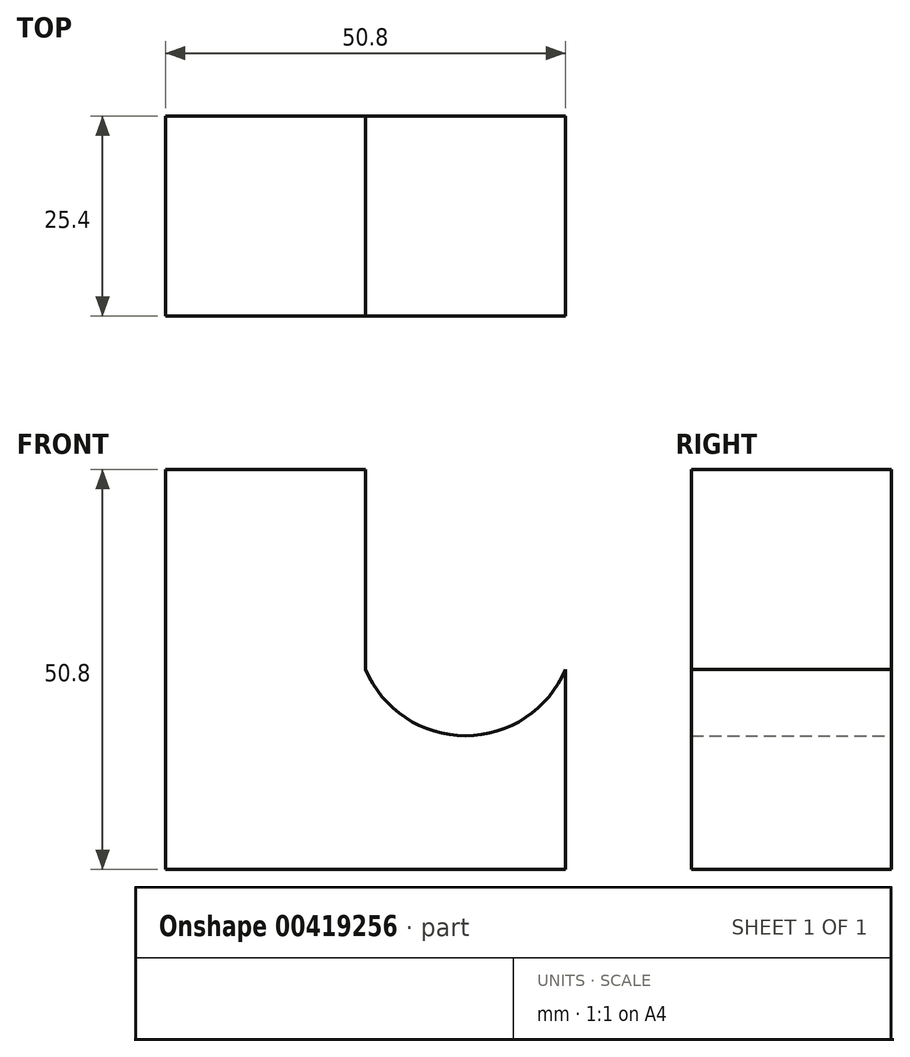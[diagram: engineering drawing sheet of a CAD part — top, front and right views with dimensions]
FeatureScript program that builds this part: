
annotation { "Feature Type Name" : "Feature", "Feature Type Description" : "" }
export const myFeature = defineFeature(function(context is Context, id is Id, definition is map)
    precondition{}
    {
        {
            var Q0;
            Q0=qCreatedBy(makeId("Front.planeOp"),FACE);
            var sketch = newSketch(context, id + "F0", { "sketchPlane" : qUnion([Q0])});
            skLineSegment(sketch, "E0", {"start": v(0, 0) * mm, "end": v(-50.8, 0) * mm});
            skLineSegment(sketch, "E1", {"start": v(-50.8, 0) * mm, "end": v(-50.8, 50.8) * mm});
            skLineSegment(sketch, "E2", {"start": v(-50.8, 50.8) * mm, "end": v(-25.4, 50.8) * mm});
            skLineSegment(sketch, "E3", {"start": v(-25.4, 50.8) * mm, "end": v(-25.4, 25.4) * mm});
            skLineSegment(sketch, "E4", {"start": v(0, 25.4) * mm, "end": v(0, 0) * mm});
            skArc(sketch, "E5", {"start": v(-25.4, 25.4) * mm, "mid": v(-12.7, 16.98) * mm, "end": v(0, 25.4) * mm});
            skSolve(sketch);
        }
        {
            var Q0;
            Q0=makeQuery(id+"F0.imprint","IMPRINT",FACE,{"disambiguationData":[TD([[makeQuery(id+"F0.imprint","IMPRINT",EDGE,{"derivedFrom":sQuery(id+"F0.wireOp",EDGE,"E0")}),-1.0]])]});
            extrude(context, id + "F1", {"entities" : qUnion([Q0]), "depth" : 25.4 * mm});
        }
    });
